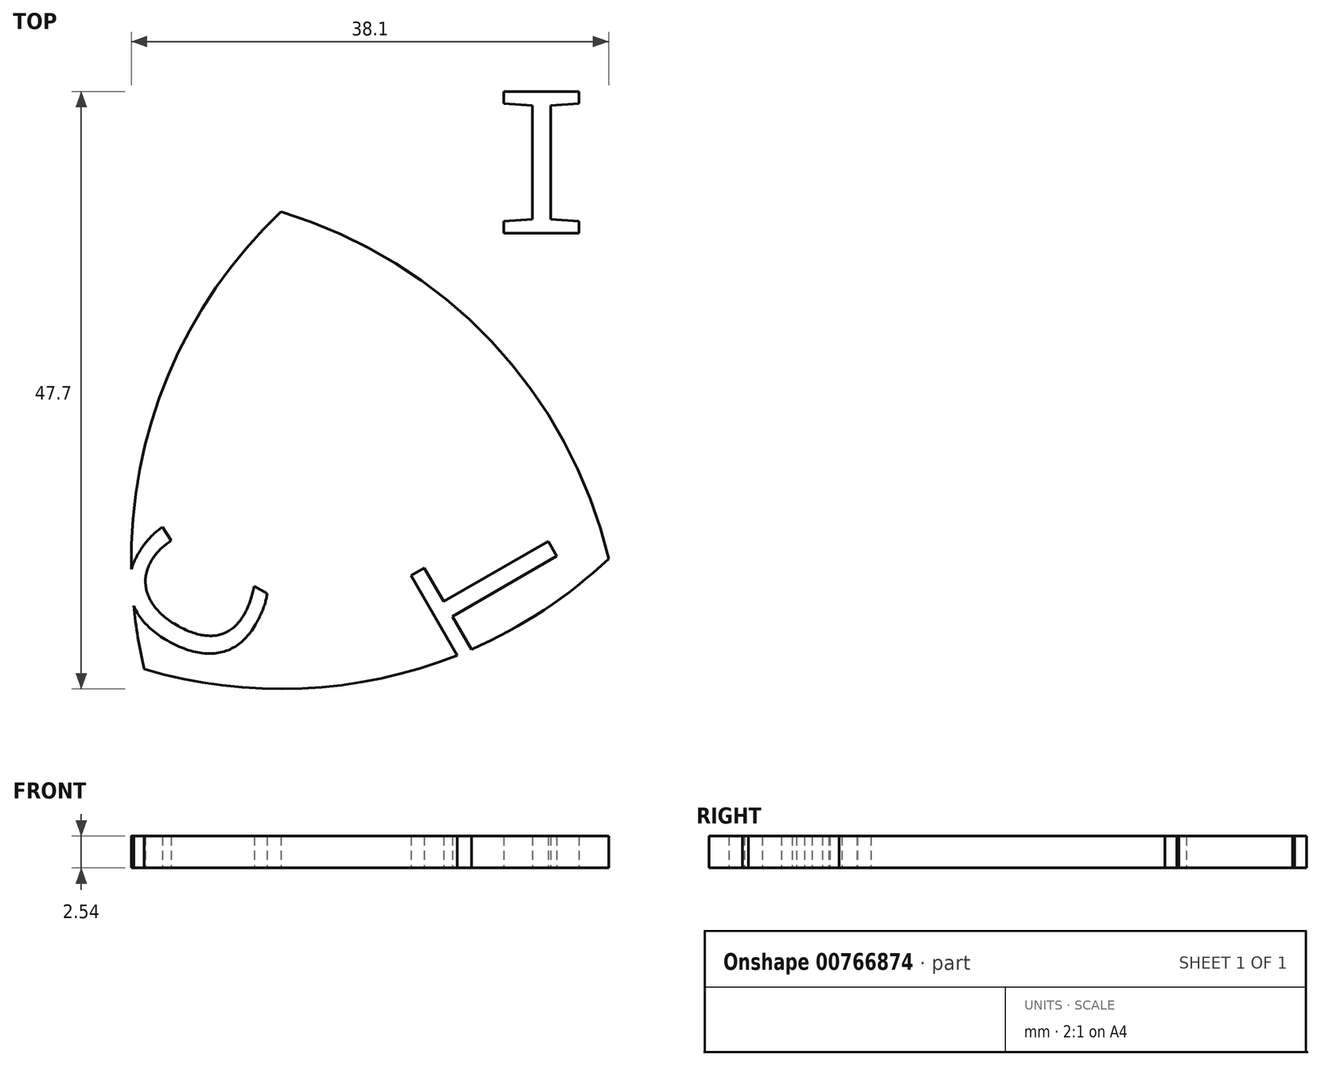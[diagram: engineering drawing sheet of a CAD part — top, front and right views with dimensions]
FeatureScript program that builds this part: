
annotation { "Feature Type Name" : "Feature", "Feature Type Description" : "" }
export const myFeature = defineFeature(function(context is Context, id is Id, definition is map)
    precondition{}
    {
        {
            var Q0;
            Q0=qCreatedBy(makeId("Top.planeOp"),FACE);
            var sketch = newSketch(context, id + "F0", { "sketchPlane" : qUnion([Q0])});
            skCircle(sketch, "E0", {"center": v(0, 0) * mm, "radius": 38.1 * mm});
            skSolve(sketch);
        }
        {
            var Q0;
            Q0=qCreatedBy(makeId("Top.planeOp"),FACE);
            var sketch = newSketch(context, id + "F1", { "sketchPlane" : qUnion([Q0])});
            skCircle(sketch, "E1", {"center": v(-26.16, 27.7) * mm, "radius": 38.1 * mm});
            skSolve(sketch);
        }
        {
            var Q0;
            Q0=qCreatedBy(makeId("Top.planeOp"),FACE);
            var sketch = newSketch(context, id + "F2", { "sketchPlane" : qUnion([Q0])});
            skCircle(sketch, "E2", {"center": v(-37.07, -8.81) * mm, "radius": 38.1 * mm});
            skSolve(sketch);
        }
        {
            var Q0;
            Q0 = qSketchRegion(id + "F0", true);
            extrude(context, id + "F3", {"entities" : qUnion([Q0]), "depth" : 2.54 * mm, "offsetDistance" : 25.4 * mm});
        }
        {
            var Q0;
            Q0 = qSketchRegion(id + "F1", true);
            extrude(context, id + "F4", {"entities" : qUnion([Q0]), "depth" : 2.54 * mm, "offsetDistance" : 25.4 * mm});
        }
        {
            var Q0;
            Q0 = qSketchRegion(id + "F2", true);
            extrude(context, id + "F5", {"entities" : qUnion([Q0]), "depth" : 2.54 * mm, "offsetDistance" : 25.4 * mm});
        }
        {
            var Q0;
            Q0=makeQuery(id+"F5.opExtrude","SWEPT_BODY",BODY,{"disambiguationData":[OSD([sQuery(id+"F2.wireOp",EDGE,"E2")])]});
            var Q1;
            Q1=makeQuery(id+"F4.opExtrude","SWEPT_BODY",BODY,{"disambiguationData":[OSD([sQuery(id+"F1.wireOp",EDGE,"E1")])]});
            var Q2;
            Q2=makeQuery(id+"F3.opExtrude","SWEPT_BODY",BODY,{"disambiguationData":[OSD([sQuery(id+"F0.wireOp",EDGE,"E0")])]});
            booleanBodies(context, id + "F6", {"operationType" : BooleanOperationType.INTERSECTION, "tools" : qUnion([Q0, Q1, Q2])});
        }
        {
            var Q0;
            Q0=qCreatedBy(makeId("Top.planeOp"),FACE);
            var sketch = newSketch(context, id + "F7", { "sketchPlane" : qUnion([Q0])});
            skText(sketch, "E3", { "text": "C", "fontName": "DroidSansMono.ttf"});
            skText(sketch, "E4", { "text": "I", "fontName": "DroidSansMono.ttf"});
            skText(sketch, "E5", { "text": "T", "fontName": "DroidSansMono.ttf"});
            const initialGuessF7  = {"E3": [-0.0311, -0.01, 0.5, 0.86603, 0.01073], "E4": [-0.01011, 0.026, 1, 0, 0.0114], "E5": [-0.00221, -0.00314, -0.5, 0.86603, 0.01094]};
            skSetInitialGuess(sketch, initialGuessF7);
            skSolve(sketch);
        }
        {
            var Q0;
            Q0 = qSketchRegion(id + "F7", true);
            extrude(context, id + "F8", {"entities" : qUnion([Q0]), "depth" : 2.54 * mm, "offsetDistance" : 25.4 * mm});
        }
        {
            var Q0;
            Q0=makeQuery(id+"F8.opExtrude","SWEPT_BODY",BODY,{"disambiguationData":[OSD([sQuery(id+"F7.wireOp",EDGE,"E5.sketch_text.stroke-0"),sQuery(id+"F7.wireOp",EDGE,"E5.sketch_text.stroke-1"),sQuery(id+"F7.wireOp",EDGE,"E5.sketch_text.stroke-2"),sQuery(id+"F7.wireOp",EDGE,"E5.sketch_text.stroke-3"),sQuery(id+"F7.wireOp",EDGE,"E5.sketch_text.stroke-4"),sQuery(id+"F7.wireOp",EDGE,"E5.sketch_text.stroke-5"),sQuery(id+"F7.wireOp",EDGE,"E5.sketch_text.stroke-6"),sQuery(id+"F7.wireOp",EDGE,"E5.sketch_text.stroke-7")])]});
            var Q1;
            Q1=makeQuery(id+"F8.opExtrude","SWEPT_BODY",BODY,{"disambiguationData":[OSD([sQuery(id+"F7.wireOp",EDGE,"E3.sketch_text.stroke-0"),sQuery(id+"F7.wireOp",EDGE,"E3.sketch_text.stroke-1"),sQuery(id+"F7.wireOp",EDGE,"E3.sketch_text.stroke-2"),sQuery(id+"F7.wireOp",EDGE,"E3.sketch_text.stroke-3"),sQuery(id+"F7.wireOp",EDGE,"E3.sketch_text.stroke-4"),sQuery(id+"F7.wireOp",EDGE,"E3.sketch_text.stroke-5"),sQuery(id+"F7.wireOp",EDGE,"E3.sketch_text.stroke-6"),sQuery(id+"F7.wireOp",EDGE,"E3.sketch_text.stroke-7"),sQuery(id+"F7.wireOp",EDGE,"E3.sketch_text.stroke-8"),sQuery(id+"F7.wireOp",EDGE,"E3.sketch_text.stroke-9"),sQuery(id+"F7.wireOp",EDGE,"E3.sketch_text.stroke-10"),sQuery(id+"F7.wireOp",EDGE,"E3.sketch_text.stroke-11"),sQuery(id+"F7.wireOp",EDGE,"E3.sketch_text.stroke-12"),sQuery(id+"F7.wireOp",EDGE,"E3.sketch_text.stroke-13")])]});
            var Q2;
            Q2=makeQuery(id+"F6.opBoolean","INTERSECT",BODY,{"derivedFrom":[makeQuery(id+"F3.opExtrude","SWEPT_BODY",BODY,{"disambiguationData":[OSD([sQuery(id+"F0.wireOp",EDGE,"E0")])]}),makeQuery(id+"F4.opExtrude","SWEPT_BODY",BODY,{"disambiguationData":[OSD([sQuery(id+"F1.wireOp",EDGE,"E1")])]}),makeQuery(id+"F5.opExtrude","SWEPT_BODY",BODY,{"disambiguationData":[OSD([sQuery(id+"F2.wireOp",EDGE,"E2")])]})]});
            booleanBodies(context, id + "F9", {"operationType" : BooleanOperationType.SUBTRACTION, "tools" : qUnion([Q0, Q1]), "targets" : qUnion([Q2])});
        }
    });
